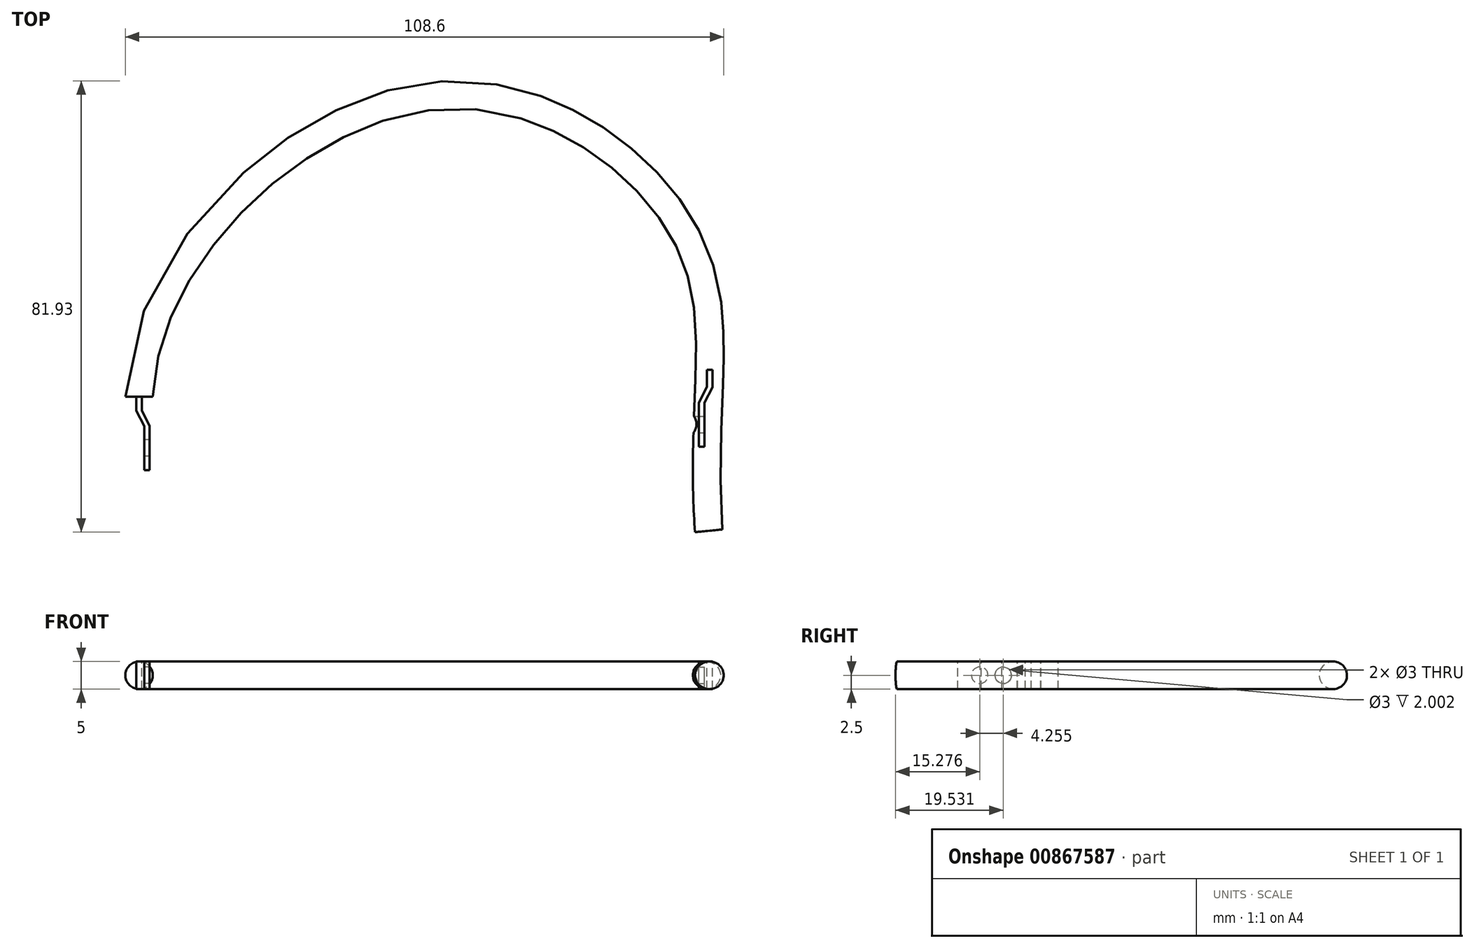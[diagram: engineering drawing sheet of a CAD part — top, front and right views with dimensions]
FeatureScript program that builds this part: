
annotation { "Feature Type Name" : "Feature", "Feature Type Description" : "" }
export const myFeature = defineFeature(function(context is Context, id is Id, definition is map)
    precondition{}
    {
        {
            var Q0;
            Q0=qCreatedBy(makeId("Top.planeOp"),FACE);
            var sketch = newSketch(context, id + "F0", { "sketchPlane" : qUnion([Q0])});
            skLineSegment(sketch, "E0", {"start": v(-80.1, 0) * mm, "end": v(80.1, 0) * mm, "construction": true});
            skLineSegment(sketch, "E1", {"start": v(0, 54.6) * mm, "end": v(0, 0) * mm, "construction": true});
            skPoint(sketch, "E1.startSnap0", {"position": v(0, 0) * mm});
            skLineSegment(sketch, "E2", {"start": v(-62.28, 54.6) * mm, "end": v(51.9, 54.6) * mm, "construction": true});
            skFitSpline(sketch, "E3", {"points": [v(-53, 0) * mm, v(0, 54.6) * mm, v(46.88, 28.11) * mm, v(50.38, -24.35) * mm], "startDerivative": vector(5.52, 204.01) * mm, "endDerivative": vector(16.21, -234.9) * mm});
            skSolve(sketch);
        }
        {
            var Q0;
            Q0=qCreatedBy(makeId("Front.planeOp"),FACE);
            var sketch = newSketch(context, id + "F1", { "sketchPlane" : qUnion([Q0])});
            skCircle(sketch, "E4", {"center": v(-53, 0) * mm, "radius": 2.5 * mm});
            skSolve(sketch);
        }
        {
            var Q0;
            Q0=makeQuery(id+"F1.imprint","IMPRINT",FACE,{"disambiguationData":[TD([[makeQuery(id+"F1.imprint","IMPRINT",EDGE,{"derivedFrom":sQuery(id+"F1.wireOp",EDGE,"E4")}),1.0]])]});
            var Q1;
            Q1=sQuery(id+"F0.wireOp",EDGE,"E3");
            sweep(context, id + "F2", {"profiles" : qUnion([Q0]), "path" : qUnion([Q1])});
        }
        {
            var Q0;
            Q0=qCreatedBy(makeId("Top.planeOp"),FACE);
            cPlane(context, id + "F3", {"entities" : qUnion([Q0]), "cplaneType" : CPlaneType.OFFSET, "offset" : 2.5 * mm, "width" : 150 * mm, "height" : 150 * mm});
        }
        {
            var Q0;
            Q0=qCreatedBy(id+"F3.planeOp",FACE);
            var sketch = newSketch(context, id + "F4", { "sketchPlane" : qUnion([Q0])});
            skLineSegment(sketch, "E5.MirrorCS", {"start": v(-52.5, 0) * mm, "end": v(-53.5, 0) * mm});
            skLineSegment(sketch, "E6.MirrorCS", {"start": v(-52.08, -13.31) * mm, "end": v(-51.08, -13.31) * mm});
            skLineSegment(sketch, "E7.MirrorCS", {"start": v(-53.5, -2.53) * mm, "end": v(-52.08, -5.31) * mm});
            skLineSegment(sketch, "E8.MirrorCS", {"start": v(-53.5, 0) * mm, "end": v(-53.5, -2.53) * mm});
            skLineSegment(sketch, "E9.MirrorCS", {"start": v(-52.5, 0) * mm, "end": v(-52.5, -2.46) * mm});
            skLineSegment(sketch, "E10.MirrorCS", {"start": v(-51.08, -5.31) * mm, "end": v(-52.5, -2.46) * mm});
            skLineSegment(sketch, "E11.MirrorCS", {"start": v(-51.08, -13.31) * mm, "end": v(-51.08, -5.31) * mm});
            skLineSegment(sketch, "E12.MirrorCS", {"start": v(-52.08, -5.31) * mm, "end": v(-52.08, -13.31) * mm});
            skLineSegment(sketch, "E13.MirrorCS", {"start": v(50.05, 4.9) * mm, "end": v(51.04, 4.9) * mm});
            skLineSegment(sketch, "E14.MirrorCS", {"start": v(48.62, -1.06) * mm, "end": v(50.05, 1.8) * mm});
            skLineSegment(sketch, "E15.MirrorCS", {"start": v(51.04, 1.72) * mm, "end": v(49.62, -1.06) * mm});
            skLineSegment(sketch, "E16.MirrorCS", {"start": v(51.04, 4.9) * mm, "end": v(51.04, 1.72) * mm});
            skLineSegment(sketch, "E17.MirrorCS", {"start": v(50.05, 4.9) * mm, "end": v(50.05, 1.8) * mm});
            skLineSegment(sketch, "E18.MirrorCS", {"start": v(49.62, -9.06) * mm, "end": v(48.62, -9.06) * mm});
            skLineSegment(sketch, "E19.MirrorCS", {"start": v(48.62, -9.06) * mm, "end": v(48.62, -1.06) * mm});
            skLineSegment(sketch, "E20.MirrorCS", {"start": v(49.62, -1.06) * mm, "end": v(49.62, -9.06) * mm});
            skSolve(sketch);
        }
        {
            var Q0;
            Q0 = qSketchRegion(id + "F4", true);
            extrude(context, id + "F5", {"entities" : qUnion([Q0]), "oppositeDirection" : true, "depth" : 5 * mm, "offsetDistance" : 25 * mm});
        }
        {
            var Q0;
            Q0=makeQuery(id+"F5.opExtrude","SWEPT_FACE",FACE,{"disambiguationData":[OSD([sQuery(id+"F4.wireOp",EDGE,"E12.MirrorCS")])]});
            var sketch = newSketch(context, id + "F6", { "sketchPlane" : qUnion([Q0])});
            skCircle(sketch, "E21", {"center": v(9.31, 0) * mm, "radius": 1.5 * mm});
            skPoint(sketch, "E21.centerSnap0", {"position": v(13.31, 0) * mm});
            skPoint(sketch, "E21.centerSnap1", {"position": v(9.31, 2.5) * mm});
            skSolve(sketch);
        }
        {
            var Q0;
            Q0 = qSketchRegion(id + "F6", true);
            extrude(context, id + "F7", {"entities" : qUnion([Q0]), "operationType" : NewBodyOperationType.REMOVE, "oppositeDirection" : true, "depth" : 25 * mm, "offsetDistance" : 25 * mm});
        }
        {
            var Q0;
            Q0=makeQuery(id+"F5.opExtrude","SWEPT_FACE",FACE,{"disambiguationData":[OSD([sQuery(id+"F4.wireOp",EDGE,"E20.MirrorCS")])]});
            var sketch = newSketch(context, id + "F8", { "sketchPlane" : qUnion([Q0])});
            skCircle(sketch, "E22", {"center": v(-5.06, 0) * mm, "radius": 1.5 * mm});
            skPoint(sketch, "E22.centerSnap0", {"position": v(-9.06, 0) * mm});
            skPoint(sketch, "E22.centerSnap1", {"position": v(-5.06, 2.5) * mm});
            skSolve(sketch);
        }
        {
            var Q0;
            Q0 = qSketchRegion(id + "F8", true);
            extrude(context, id + "F9", {"entities" : qUnion([Q0]), "operationType" : NewBodyOperationType.REMOVE, "oppositeDirection" : true, "depth" : 25 * mm, "offsetDistance" : 25 * mm});
        }
    });
